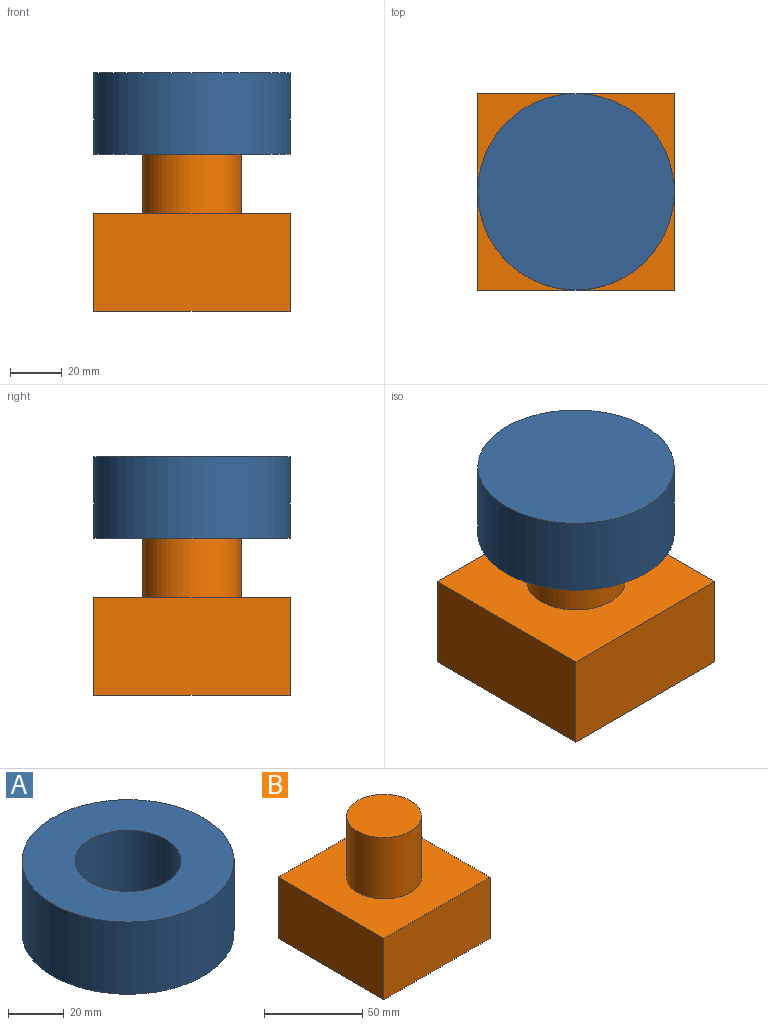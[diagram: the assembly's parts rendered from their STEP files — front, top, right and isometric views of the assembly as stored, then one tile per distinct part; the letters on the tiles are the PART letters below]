
ASSEMBLY  parts=2 mates=1
PART A: 5 faces, bbox 76.2x76.2x31.8 mm
  f0: cylinder r=38.1mm len=76.2mm, axis (0,0,-1), area 7600.6mm2, adj f1,f2
  f1: plane 76.2x76.2mm, normal (0,0,1), area 3420.3mm2, adj f0,f3
  f2: plane 76.2x76.2mm, normal (0,0,-1), area 4560.4mm2, adj f0
  f3: cylinder r=19.05mm len=38.1mm, axis (0,0,1), area 3648.3mm2, adj f1,f4
  f4: plane 38.1x38.1mm, normal (0,0,1), area 1140.1mm2, adj f3
PART B: 8 faces, bbox 76.2x76.2x76.2 mm
  f0: plane 76.2x38.1mm, normal (0,1,0), area 2903.2mm2, adj f1,f3,f4,f5
  f1: plane 76.2x38.1mm, normal (-1,0,0), area 2903.2mm2, adj f0,f2,f4,f5
  f2: plane 76.2x38.1mm, normal (0,-1,0), area 2903.2mm2, adj f1,f3,f4,f5
  f3: plane 76.2x38.1mm, normal (1,0,0), area 2903.2mm2, adj f0,f2,f4,f5
  f4: plane 76.2x76.2mm, normal (0,0,1), area 4666.3mm2, adj f0,f1,f2,f3,f6
  f5: plane 76.2x76.2mm, normal (0,0,-1), area 5806.4mm2, adj f0,f1,f2,f3
  f6: cylinder r=19.05mm len=38.1mm, axis (0,0,-1), area 4560.4mm2, adj f4,f7
  f7: plane 38.1x38.1mm, normal (0,0,1), area 1140.1mm2, adj f6
PLACE A rot(axis=(0,1,0),180deg) t=(16.08,-65.93,117.79)mm
PLACE B t=(-22.02,-27.83,25.08)mm
MATE revolute A.f3 <-> B.f6  axis (0,0,-1) through (16.08,-65.93,101.28)mm
